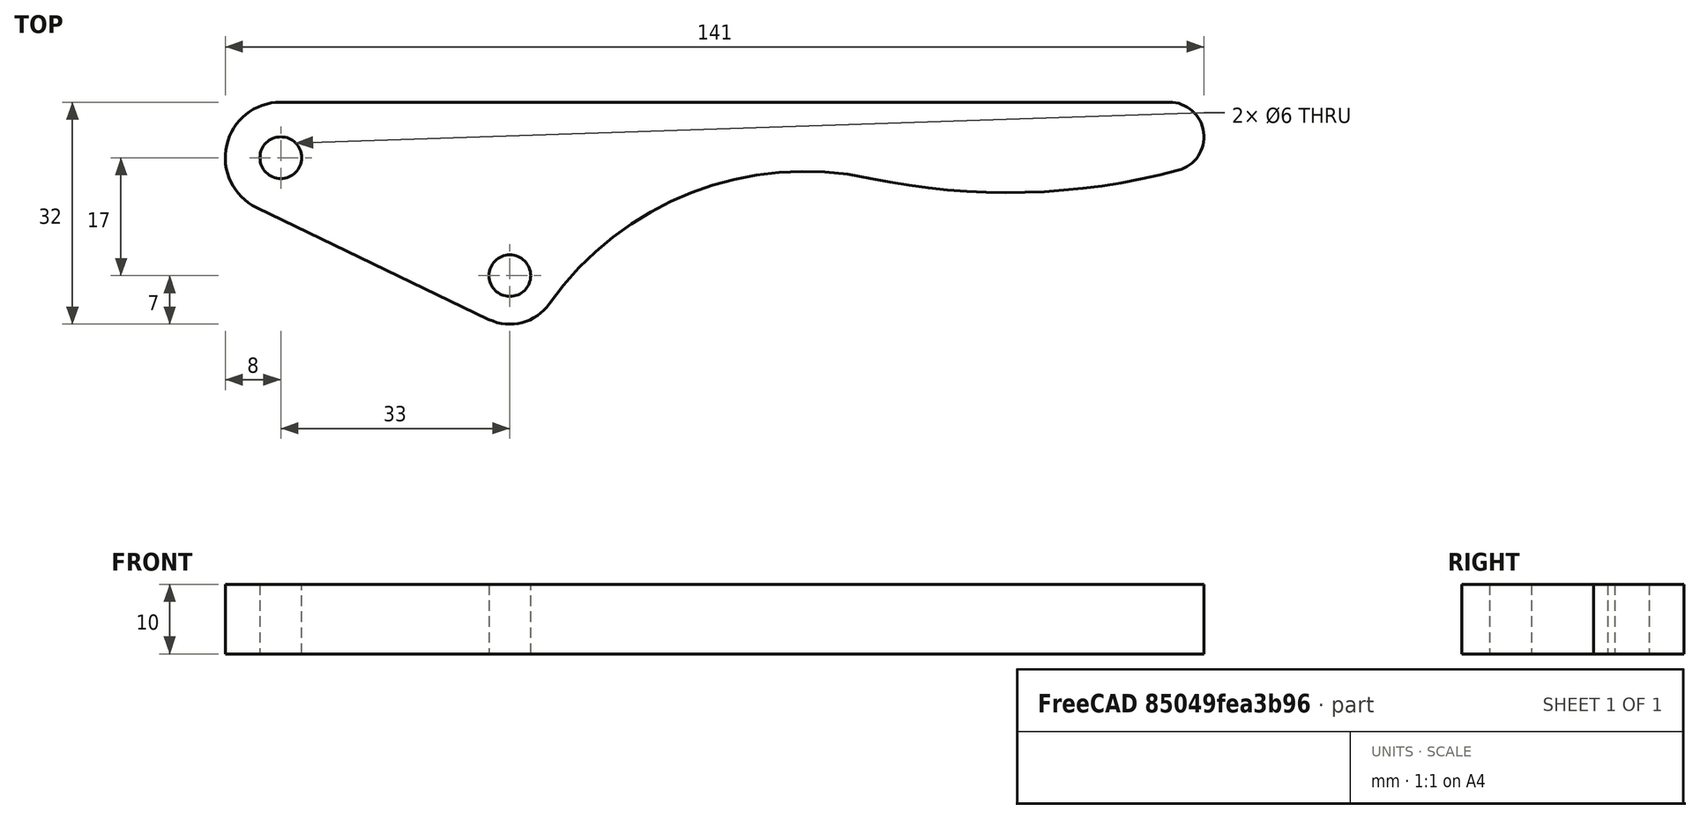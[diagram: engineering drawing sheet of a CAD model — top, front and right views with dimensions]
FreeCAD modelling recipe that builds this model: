
FCSTD DOCUMENT  (FreeCAD 0.19R23756 (Git))
Label: CLAMP_4
License: All rights reserved
LicenseURL: http://en.wikipedia.org/wiki/All_rights_reserved
objects: Sketcher::SketchObject×1, PartDesign::Pad×1, PartDesign::Body×1
note: 4 computed .brp shape members not serialized (recipe doc carries the construction recipe); baked Part::Feature solids carry a one-line shape summary decoded from their .brp

FEATURE [Sketcher::SketchObject] Sketch
  FullyConstrained = true
  MapMode = 5
  Support = -> [XY_Plane]
  sketch-geometry (9):
    g0: LineSegment StartX=128 StartY=8 StartZ=0 EndX=0 EndY=8 EndZ=0
    g1: ArcOfCircle CenterX=0 CenterY=0 CenterZ=0 NormalX=0 NormalY=0 NormalZ=1 AngleXU=0 Radius=8 StartAngle=1.5708 EndAngle=4.26364
    g2: LineSegment StartX=-3.47074 StartY=-7.20791 StartZ=0 EndX=29.9631 EndY=-23.3069 EndZ=0
    g3: ArcOfCircle CenterX=33 CenterY=-17 CenterZ=0 NormalX=0 NormalY=0 NormalZ=1 AngleXU=0 Radius=7 StartAngle=4.26364 EndAngle=5.66864
    g4: ArcOfCircle CenterX=75.4857 CenterY=-46.9827 CenterZ=0 NormalX=0 NormalY=0 NormalZ=1 AngleXU=0 Radius=45 StartAngle=1.35776 EndAngle=2.52704
    g5: ArcOfCircle CenterX=104.68 CenterY=90.9612 CenterZ=0 NormalX=0 NormalY=0 NormalZ=1 AngleXU=0 Radius=96 StartAngle=4.50593 EndAngle=4.97155
    g6: ArcOfCircle CenterX=128 CenterY=3 CenterZ=0 NormalX=0 NormalY=0 NormalZ=1 AngleXU=0 Radius=5 StartAngle=4.97155 EndAngle=7.85398
    g7: Circle CenterX=33 CenterY=-17 CenterZ=0 NormalX=0 NormalY=0 NormalZ=1 AngleXU=0 Radius=3
    g8: Circle CenterX=0 CenterY=0 CenterZ=0 NormalX=0 NormalY=0 NormalZ=1 AngleXU=0 Radius=3
  constraints (25):
    c: Tangent(g0,g1) = -1.5708
    c: Tangent(g1,g2) = -1.5708
    c: Tangent(g2,g3) = -1.5708
    c: Tangent(g3,g4) = 1.5708
    c: Coincident(g-1,g1)
    c: Radius(g1) = 8
    c: Radius(g3) = 7
    c: DistanceX(g4) = 85
    c: DistanceY(g4) = -3
    c: Radius(g4) = 45
    c: DistanceX(g0) = 128
    c: Coincident(g5,g4)
    c: Radius(g5) = 96
    c: Coincident(g6,g0)
    c: Coincident(g6,g5)
    c: Radius(g6) = 5
    c: Tangent(g5,g6)
    c: Tangent(g0,g6)
    c: Coincident(g7,g3)
    c: Coincident(g8,g1)
    c: Diameter(g8) = 6
    c: Equal(g8,g7)
    c: Horizontal(g0)
    c: DistanceY(g3,g1) = 17
    c: DistanceX(g1,g3) = 33
FEATURE [PartDesign::Pad] Pad
  AllowMultiFace = false
  Direction = (1,1,1)
  Length = 10
  Length2 = 100
  Profile = -> Sketch
  Type = 0
FEATURE [PartDesign::Body] Body
  Group = -> [Sketch,Pad]
  Origin = -> Origin
  Tip = -> Pad
